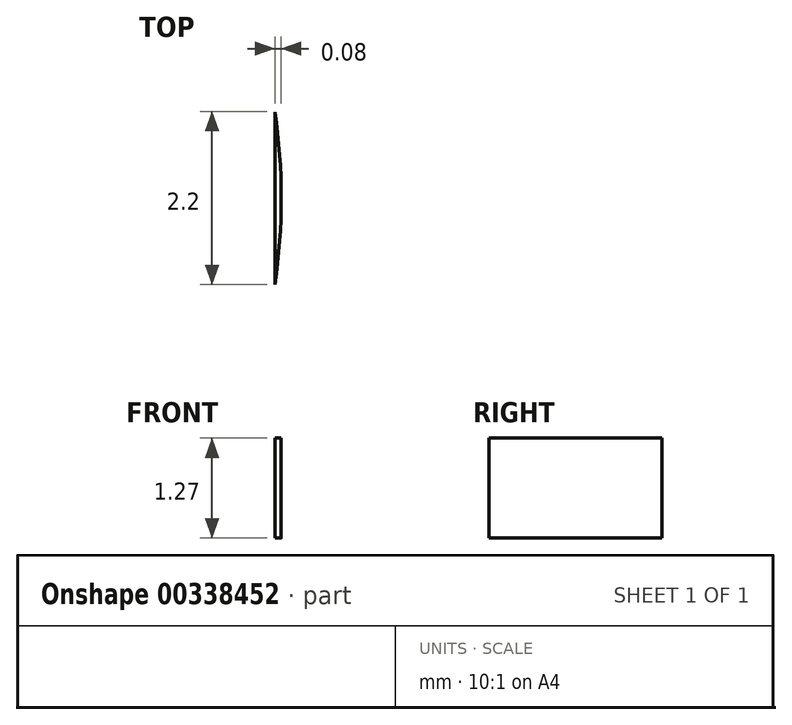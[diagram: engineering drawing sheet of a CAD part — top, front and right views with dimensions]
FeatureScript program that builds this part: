
annotation { "Feature Type Name" : "Feature", "Feature Type Description" : "" }
export const myFeature = defineFeature(function(context is Context, id is Id, definition is map)
    precondition{}
    {
        {
            var Q0;
            Q0=qCreatedBy(makeId("Top.planeOp"),FACE);
            var sketch = newSketch(context, id + "F0", { "sketchPlane" : qUnion([Q0])});
            skArc(sketch, "E0", {"start": v(7.54, 24.78) * mm, "mid": v(0.46, 33.49) * mm, "end": v(-7.62, 25.7) * mm});
            skArc(sketch, "E1", {"start": v(-7.62, -14.58) * mm, "mid": v(0.46, -22.37) * mm, "end": v(7.54, -13.66) * mm});
            skLineSegment(sketch, "E2", {"start": v(7.54, 26.98) * mm, "end": v(7.54, -15.86) * mm});
            skLineSegment(sketch, "E3", {"start": v(-7.62, 26.06) * mm, "end": v(-7.62, -14.94) * mm});
            skSolve(sketch);
        }
        {
            var Q0;
            {var subQ0=sQuery(id+"F0.wireOp",EDGE,"E2");var subQ1=sQuery(id+"F0.wireOp",EDGE,"E0");var subQ8=makeQuery(id+"F0.imprint","INTERSECT",VERTEX,{"disambiguationData":[OD(1.0)],"derivedFrom":[subQ1,subQ0]});Q0=makeQuery(id+"F0.imprint","IMPRINT",FACE,{"disambiguationData":[TD([[makeQuery(id+"F0.imprint","IMPRINT",EDGE,{"disambiguationData":[TD([[subQ8,-1.0]])],"derivedFrom":subQ1}),1.0]])]});}
            extrude(context, id + "F1", {"entities" : qUnion([Q0]), "depth" : 1.27 * mm});
        }
        {
            var Q0;
            Q0=makeQuery(id+"F1.opExtrude","CAP_FACE",FACE,{"disambiguationData":[OSD([sQuery(id+"F0.wireOp",EDGE,"E0"),sQuery(id+"F0.wireOp",EDGE,"E1"),sQuery(id+"F0.wireOp",EDGE,"E2"),sQuery(id+"F0.wireOp",EDGE,"E3")])],"isStart":false});
            var sketch = newSketch(context, id + "F2", { "sketchPlane" : qUnion([Q0])});
            skPoint(sketch, "E4", {"position": v(0, 25.88) * mm});
            skPoint(sketch, "E5", {"position": v(0, -14.76) * mm});
            skCircle(sketch, "E6", {"center": v(0, 25.88) * mm, "radius": 3.18 * mm});
            skCircle(sketch, "E7", {"center": v(0, -14.76) * mm, "radius": 3.18 * mm});
            skSolve(sketch);
        }
        {
            var Q0;
            Q0=makeQuery(id+"F2.imprint","IMPRINT",FACE,{"disambiguationData":[TD([[makeQuery(id+"F2.imprint","IMPRINT",EDGE,{"derivedFrom":sQuery(id+"F2.wireOp",EDGE,"E6")}),1.0]])]});
            var Q1;
            Q1=makeQuery(id+"F2.imprint","IMPRINT",FACE,{"disambiguationData":[TD([[makeQuery(id+"F2.imprint","IMPRINT",EDGE,{"derivedFrom":sQuery(id+"F2.wireOp",EDGE,"E7")}),1.0]])]});
            extrude(context, id + "F3", {"entities" : qUnion([Q0, Q1]), "operationType" : NewBodyOperationType.REMOVE, "oppositeDirection" : true, "depth" : 25.4 * mm});
        }
    });
